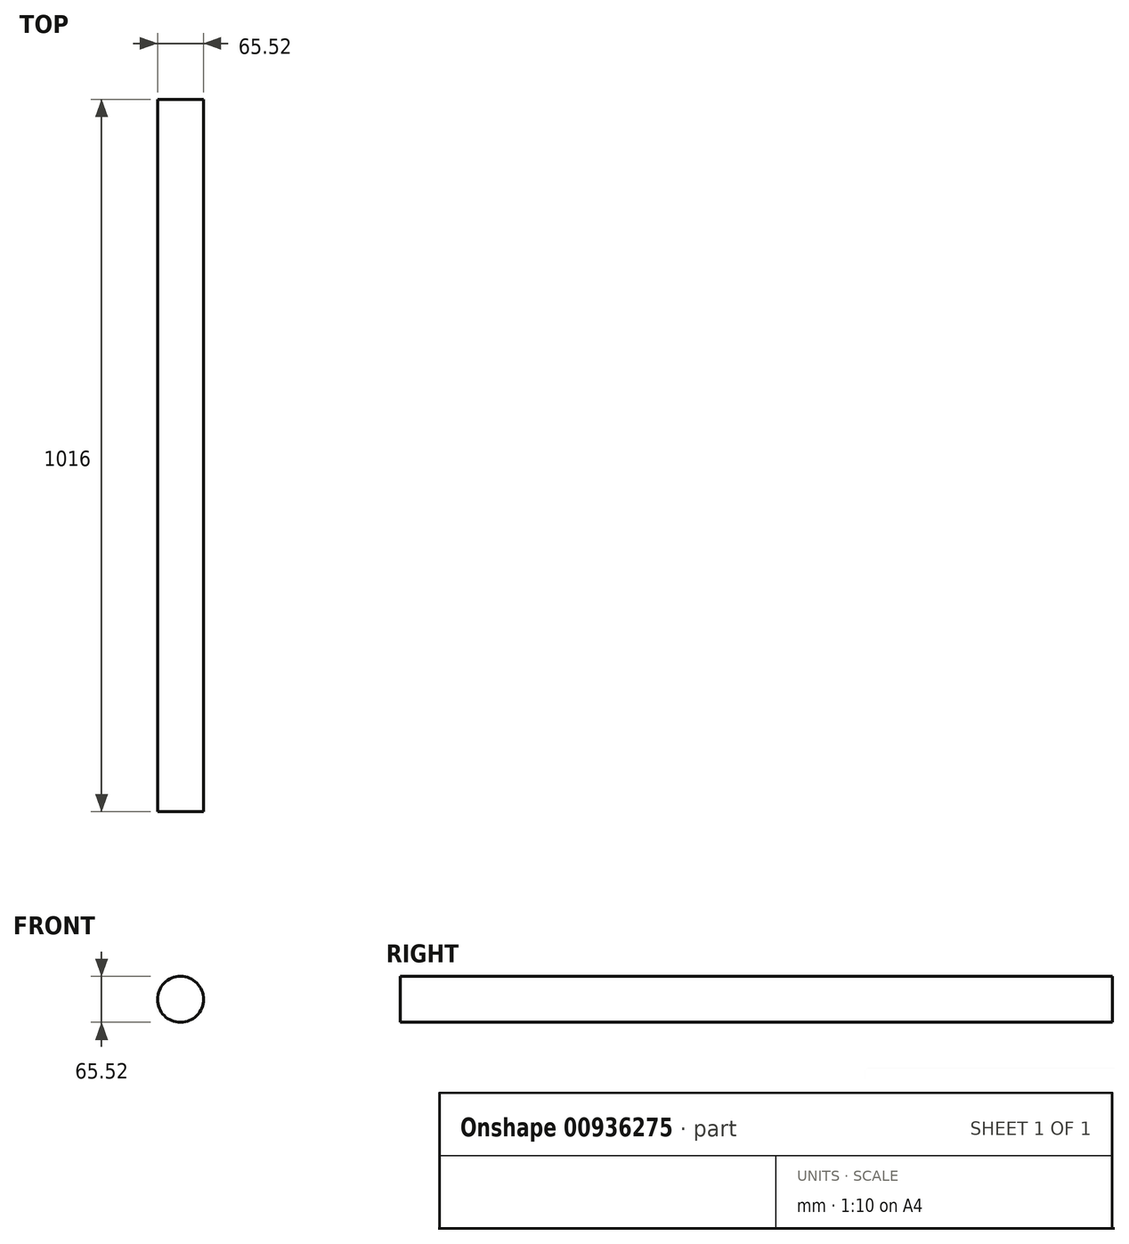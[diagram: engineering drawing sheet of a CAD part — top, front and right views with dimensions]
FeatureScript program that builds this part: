
annotation { "Feature Type Name" : "Feature", "Feature Type Description" : "" }
export const myFeature = defineFeature(function(context is Context, id is Id, definition is map)
    precondition{}
    {
        {
            var Q0;
            Q0=qCreatedBy(makeId("Front.planeOp"),FACE);
            var sketch = newSketch(context, id + "F0", { "sketchPlane" : qUnion([Q0])});
            skCircle(sketch, "E0", {"center": v(0, 0) * mm, "radius": 32.76 * mm});
            skSolve(sketch);
        }
        {
            var Q0;
            Q0=makeQuery(id+"F0.imprint","IMPRINT",FACE,{"disambiguationData":[TD([[makeQuery(id+"F0.imprint","IMPRINT",EDGE,{"derivedFrom":sQuery(id+"F0.wireOp",EDGE,"E0")}),1.0]])]});
            extrude(context, id + "F1", {"entities" : qUnion([Q0]), "depth" : 1016 * mm, "offsetDistance" : 25.4 * mm});
        }
    });
